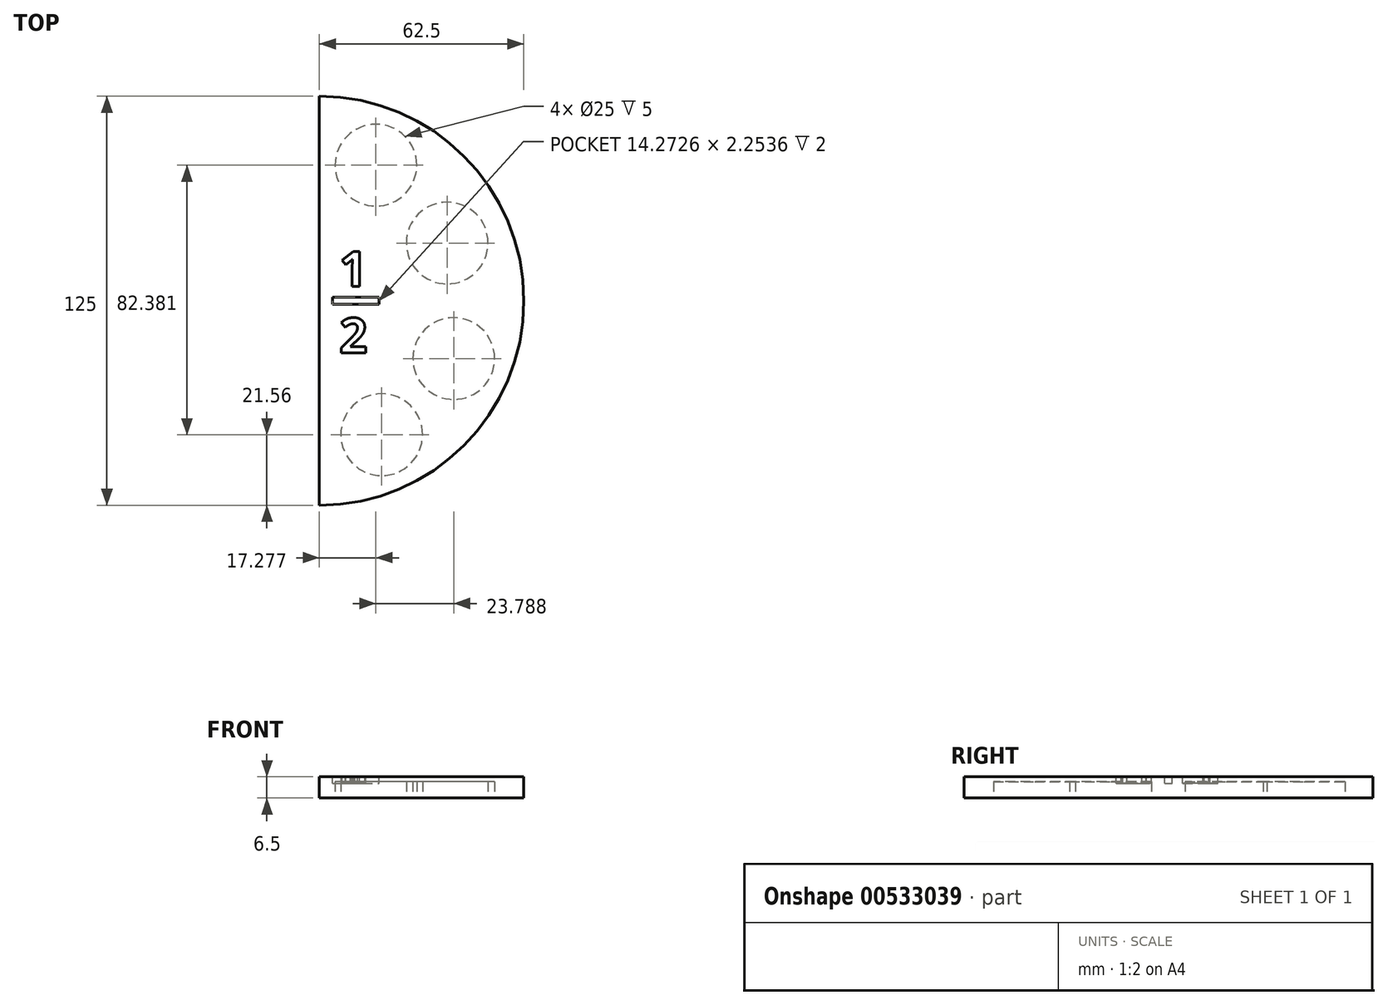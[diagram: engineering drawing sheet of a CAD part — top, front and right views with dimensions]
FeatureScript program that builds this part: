
annotation { "Feature Type Name" : "Feature", "Feature Type Description" : "" }
export const myFeature = defineFeature(function(context is Context, id is Id, definition is map)
    precondition{}
    {
        {
            var Q0;
            Q0=qCreatedBy(makeId("Top.planeOp"),FACE);
            var sketch = newSketch(context, id + "F0", { "sketchPlane" : qUnion([Q0])});
            skArc(sketch, "E0", {"start": v(0, -62.5) * mm, "mid": v(62.5, 0) * mm, "end": v(0, 62.5) * mm});
            skLineSegment(sketch, "E1", {"start": v(0, 62.5) * mm, "end": v(0, -62.5) * mm});
            skSolve(sketch);
        }
        {
            var Q0;
            Q0=makeQuery(id+"F0.imprint","IMPRINT",FACE,{"disambiguationData":[TD([[makeQuery(id+"F0.imprint","IMPRINT",EDGE,{"derivedFrom":sQuery(id+"F0.wireOp",EDGE,"E0")}),1.0]])]});
            extrude(context, id + "F1", {"entities" : qUnion([Q0]), "depth" : 6.5 * mm, "offsetDistance" : 25 * mm});
        }
        {
            var Q0;
            Q0=makeQuery(id+"F1.opExtrude","CAP_FACE",FACE,{"disambiguationData":[OSD([sQuery(id+"F0.wireOp",EDGE,"E0"),sQuery(id+"F0.wireOp",EDGE,"E1")])],"isStart":false});
            var sketch = newSketch(context, id + "F2", { "sketchPlane" : qUnion([Q0])});
            skCircle(sketch, "E2", {"center": v(17.28, 41.44) * mm, "radius": 12.5 * mm});
            skSolve(sketch);
        }
        {
            var Q0;
            Q0=makeQuery(id+"F2.imprint","IMPRINT",FACE,{"disambiguationData":[TD([[makeQuery(id+"F2.imprint","IMPRINT",EDGE,{"derivedFrom":sQuery(id+"F2.wireOp",EDGE,"E2")}),-1.0]])]});
            var sketch = newSketch(context, id + "F3", { "sketchPlane" : qUnion([Q0])});
            skCircle(sketch, "E3", {"center": v(39.06, 17.65) * mm, "radius": 12.5 * mm});
            skSolve(sketch);
        }
        {
            var Q0;
            Q0=makeQuery(id+"F2.imprint","IMPRINT",FACE,{"disambiguationData":[TD([[makeQuery(id+"F2.imprint","IMPRINT",EDGE,{"derivedFrom":sQuery(id+"F2.wireOp",EDGE,"E2")}),-1.0]])]});
            var sketch = newSketch(context, id + "F4", { "sketchPlane" : qUnion([Q0])});
            skCircle(sketch, "E4", {"center": v(41.07, -17.65) * mm, "radius": 12.5 * mm});
            skSolve(sketch);
        }
        {
            var Q0;
            Q0=makeQuery(id+"F2.imprint","IMPRINT",FACE,{"disambiguationData":[TD([[makeQuery(id+"F2.imprint","IMPRINT",EDGE,{"derivedFrom":sQuery(id+"F2.wireOp",EDGE,"E2")}),-1.0]])]});
            var sketch = newSketch(context, id + "F5", { "sketchPlane" : qUnion([Q0])});
            skCircle(sketch, "E5", {"center": v(19.03, -40.94) * mm, "radius": 12.5 * mm});
            skSolve(sketch);
        }
        {
            var Q0;
            Q0 = qSketchRegion(id + "F2", true);
            extrude(context, id + "F6", {"entities" : qUnion([Q0]), "operationType" : NewBodyOperationType.REMOVE, "oppositeDirection" : true, "depth" : 5 * mm, "offsetDistance" : 25 * mm});
        }
        {
            var Q0;
            Q0 = qSketchRegion(id + "F3", true);
            extrude(context, id + "F7", {"entities" : qUnion([Q0]), "operationType" : NewBodyOperationType.REMOVE, "oppositeDirection" : true, "depth" : 5 * mm, "offsetDistance" : 25 * mm});
        }
        {
            var Q0;
            Q0 = qSketchRegion(id + "F4", true);
            extrude(context, id + "F8", {"entities" : qUnion([Q0]), "operationType" : NewBodyOperationType.REMOVE, "oppositeDirection" : true, "depth" : 5 * mm, "offsetDistance" : 25 * mm});
        }
        {
            var Q0;
            Q0 = qSketchRegion(id + "F5", true);
            extrude(context, id + "F9", {"entities" : qUnion([Q0]), "operationType" : NewBodyOperationType.REMOVE, "oppositeDirection" : true, "depth" : 5 * mm, "offsetDistance" : 25 * mm});
        }
        {
            var Q0;
            Q0=makeQuery(id+"F0.imprint","IMPRINT",FACE,{"disambiguationData":[TD([[makeQuery(id+"F0.imprint","IMPRINT",EDGE,{"derivedFrom":sQuery(id+"F0.wireOp",EDGE,"E0")}),1.0]])]});
            var sketch = newSketch(context, id + "F10", { "sketchPlane" : qUnion([Q0])});
            skLineSegment(sketch, "E6.bottom", {"start": v(4, -1.13) * mm, "end": v(18.28, -1.13) * mm});
            skLineSegment(sketch, "E6.top", {"start": v(4, 1.13) * mm, "end": v(18.28, 1.13) * mm});
            skLineSegment(sketch, "E6.left", {"start": v(4, -1.13) * mm, "end": v(4, 1.13) * mm});
            skLineSegment(sketch, "E6.right", {"start": v(18.28, -1.13) * mm, "end": v(18.28, 1.13) * mm});
            skSolve(sketch);
        }
        {
            var Q0;
            Q0 = qSketchRegion(id + "F10", true);
            extrude(context, id + "F11", {"entities" : qUnion([Q0]), "operationType" : NewBodyOperationType.REMOVE, "depth" : 2 * mm, "offsetDistance" : 25 * mm});
        }
        {
            var Q0;
            Q0=makeQuery(id+"F0.imprint","IMPRINT",FACE,{"disambiguationData":[TD([[makeQuery(id+"F0.imprint","IMPRINT",EDGE,{"derivedFrom":sQuery(id+"F0.wireOp",EDGE,"E0")}),1.0]])]});
            var sketch = newSketch(context, id + "F12", { "sketchPlane" : qUnion([Q0])});
            skSolve(sketch);
        }
        {
            var Q0;
            Q0=makeQuery(id+"F1.opExtrude","SWEPT_BODY",BODY,{"disambiguationData":[OSD([sQuery(id+"F0.wireOp",EDGE,"E0"),sQuery(id+"F0.wireOp",EDGE,"E1")])]});
            var Q1;
            Q1=qCreatedBy(makeId("Top.planeOp"),FACE);
            mirror(context, id + "F13", {"entities" : qUnion([Q0]), "mirrorPlane" : qUnion([Q1])});
        }
        {
            var Q0;
            Q0=makeQuery(id+"F1.opExtrude","SWEPT_BODY",BODY,{"disambiguationData":[OSD([sQuery(id+"F0.wireOp",EDGE,"E0"),sQuery(id+"F0.wireOp",EDGE,"E1")])]});
            deleteBodies(context, id + "F14", {"entities" : qUnion([Q0])});
        }
        {
            var Q0;
            Q0=makeQuery(id+"F12.imprint","IMPRINT",FACE,{"disambiguationData":[TD([[makeQuery(id+"F12.imprint","IMPRINT",EDGE,{"derivedFrom":makeQuery(id+"F0.imprint","IMPRINT",EDGE,{"derivedFrom":sQuery(id+"F0.wireOp",EDGE,"E0")})}),1.0]])]});
            var sketch = newSketch(context, id + "F15", { "sketchPlane" : qUnion([Q0])});
            skText(sketch, "E7", { "text": "1\n2", "fontName": "OpenSans-Bold.ttf"});
            const initialGuessF15  = {"E7": [0.0061, 0.00438, 1, 0, 0.01078]};
            skSetInitialGuess(sketch, initialGuessF15);
            skSolve(sketch);
        }
        {
            var Q0;
            Q0 = qSketchRegion(id + "F15", true);
            extrude(context, id + "F16", {"entities" : qUnion([Q0]), "operationType" : NewBodyOperationType.REMOVE, "oppositeDirection" : true, "depth" : 2 * mm, "offsetDistance" : 25 * mm});
        }
    });
